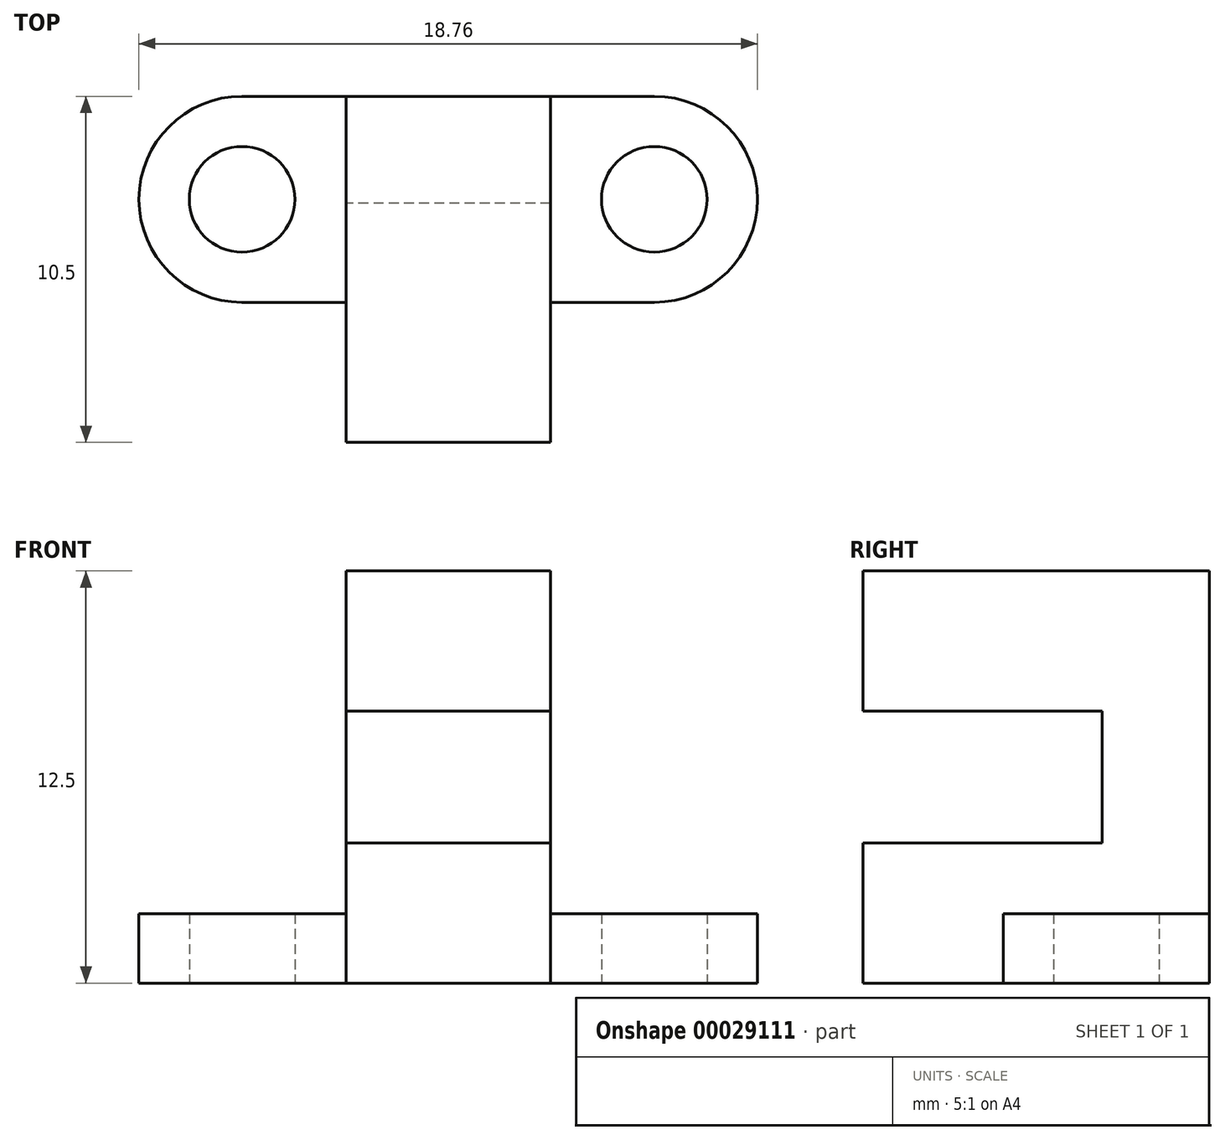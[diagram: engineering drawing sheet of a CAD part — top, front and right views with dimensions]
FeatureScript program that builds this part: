
annotation { "Feature Type Name" : "Feature", "Feature Type Description" : "" }
export const myFeature = defineFeature(function(context is Context, id is Id, definition is map)
    precondition{}
    {
        {
            var Q0;
            Q0=qCreatedBy(makeId("Right.planeOp"),FACE);
            var sketch = newSketch(context, id + "F0", { "sketchPlane" : qUnion([Q0])});
            skLineSegment(sketch, "E0", {"start": v(0, 0) * mm, "end": v(0, 12.5) * mm});
            skLineSegment(sketch, "E1", {"start": v(0, 12.5) * mm, "end": v(-10.5, 12.5) * mm});
            skLineSegment(sketch, "E2", {"start": v(-10.5, 12.5) * mm, "end": v(-10.5, 8.25) * mm});
            skLineSegment(sketch, "E3", {"start": v(-10.5, 8.25) * mm, "end": v(-3.25, 8.25) * mm});
            skLineSegment(sketch, "E4", {"start": v(-3.25, 8.25) * mm, "end": v(-3.25, 4.25) * mm});
            skLineSegment(sketch, "E5", {"start": v(-3.25, 4.25) * mm, "end": v(-10.5, 4.25) * mm});
            skLineSegment(sketch, "E6", {"start": v(-10.5, 4.25) * mm, "end": v(-10.5, 0) * mm});
            skLineSegment(sketch, "E7", {"start": v(-10.5, 0) * mm, "end": v(0, 0) * mm});
            skSolve(sketch);
        }
        {
            var Q0;
            Q0 = qSketchRegion(id + "F0", true);
            extrude(context, id + "F1", {"entities" : qUnion([Q0]), "depth" : 3.1 * mm, "hasSecondDirection" : true, "secondDirectionOppositeDirection" : true, "secondDirectionDepth" : 3.1 * mm});
        }
        {
            var Q0;
            Q0=makeQuery(id+"F1.opExtrude","SWEPT_FACE",FACE,{"disambiguationData":[OSD([sQuery(id+"F0.wireOp",EDGE,"E7")])]});
            var sketch = newSketch(context, id + "F2", { "sketchPlane" : qUnion([Q0])});
            skCircle(sketch, "E8", {"center": v(6.25, 3.12) * mm, "radius": 1.6 * mm});
            skArc(sketch, "E9", {"start": v(6.25, 0) * mm, "mid": v(9.38, 3.12) * mm, "end": v(6.25, 6.25) * mm});
            skLineSegment(sketch, "E10", {"start": v(6.25, 6.25) * mm, "end": v(3.1, 6.25) * mm});
            skLineSegment(sketch, "E11", {"start": v(6.25, 0) * mm, "end": v(3.1, 0) * mm});
            skLineSegment(sketch, "E12.MirrorCS", {"start": v(-6.25, 6.25) * mm, "end": v(-3.1, 6.25) * mm});
            skArc(sketch, "E13.MirrorCS", {"start": v(-6.25, 0) * mm, "mid": v(-9.38, 3.12) * mm, "end": v(-6.25, 6.25) * mm});
            skLineSegment(sketch, "E14.MirrorCS", {"start": v(-6.25, 0) * mm, "end": v(-3.1, 0) * mm});
            skCircle(sketch, "E15.MirrorC", {"center": v(-6.25, 3.12) * mm, "radius": 1.6 * mm});
            skSolve(sketch);
        }
        {
            var Q0;
            Q0=makeQuery(id+"F2.imprint","IMPRINT",FACE,{"disambiguationData":[TD([[makeQuery(id+"F2.imprint","IMPRINT",EDGE,{"derivedFrom":sQuery(id+"F2.wireOp",EDGE,"E8")}),-1.0]])]});
            var Q1;
            {var subQ2=sQuery(id+"F2.wireOp",EDGE,"E12.MirrorCS");Q1=makeQuery(id+"F2.imprint","IMPRINT",FACE,{"disambiguationData":[TD([[makeQuery(id+"F2.imprint","IMPRINT",EDGE,{"derivedFrom":subQ2}),-1.0]])]});}
            extrude(context, id + "F3", {"entities" : qUnion([Q0, Q1]), "operationType" : NewBodyOperationType.ADD, "oppositeDirection" : true, "depth" : 2.1 * mm});
        }
    });
